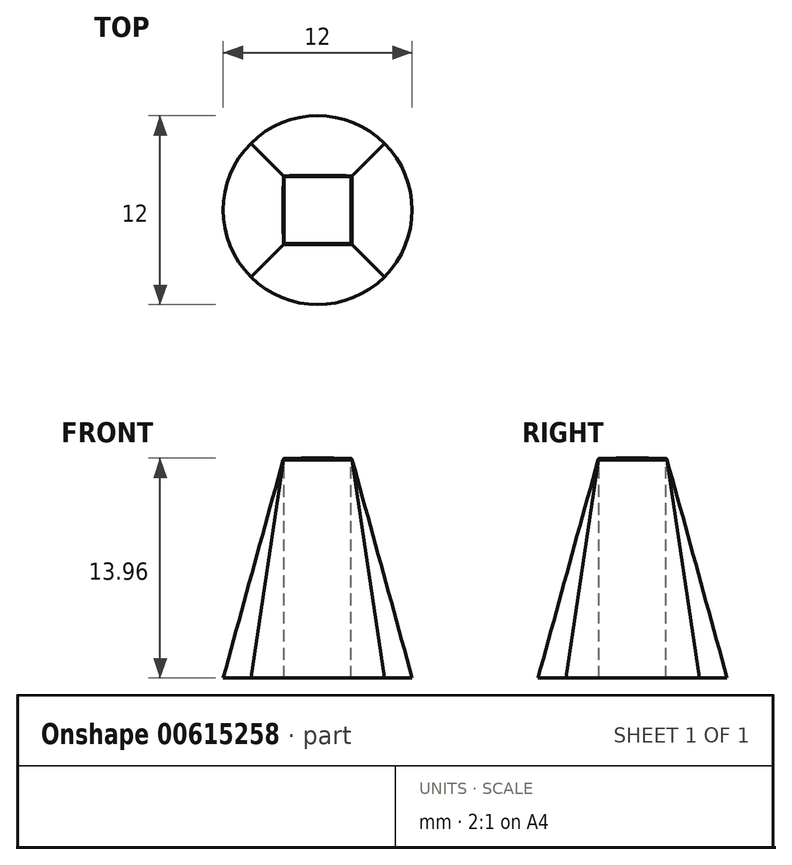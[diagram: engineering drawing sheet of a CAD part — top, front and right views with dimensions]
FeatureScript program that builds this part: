
annotation { "Feature Type Name" : "Feature", "Feature Type Description" : "" }
export const myFeature = defineFeature(function(context is Context, id is Id, definition is map)
    precondition{}
    {
        {
            var Q0;
            Q0=qCreatedBy(makeId("Top.planeOp"),FACE);
            var sketch = newSketch(context, id + "F0", { "sketchPlane" : qUnion([Q0])});
            skCircle(sketch, "E0", {"center": v(0, 0) * mm, "radius": 6 * mm});
            skSolve(sketch);
        }
        {
            var Q0;
            Q0=makeQuery(id+"F0.imprint","IMPRINT",FACE,{"disambiguationData":[TD([[makeQuery(id+"F0.imprint","IMPRINT",EDGE,{"derivedFrom":sQuery(id+"F0.wireOp",EDGE,"E0")}),1.0]])]});
            cPlane(context, id + "F1", {"entities" : qUnion([Q0]), "cplaneType" : CPlaneType.OFFSET, "offset" : 14 * mm, "width" : 150 * mm, "height" : 150 * mm});
        }
        {
            var Q0;
            Q0=qCreatedBy(id+"F1.planeOp",FACE);
            var sketch = newSketch(context, id + "F2", { "sketchPlane" : qUnion([Q0])});
            skLineSegment(sketch, "E1.bottom", {"start": v(2.15, -2.15) * mm, "end": v(-2.15, -2.15) * mm});
            skLineSegment(sketch, "E1.top", {"start": v(2.15, 2.15) * mm, "end": v(-2.15, 2.15) * mm});
            skLineSegment(sketch, "E1.left", {"start": v(2.15, -2.15) * mm, "end": v(2.15, 2.15) * mm});
            skLineSegment(sketch, "E1.right", {"start": v(-2.15, -2.15) * mm, "end": v(-2.15, 2.15) * mm});
            skPoint(sketch, "E1.middle", {"position": v(0, 0) * mm});
            skSolve(sketch);
        }
        {
            var Q0;
            Q0=makeQuery(id+"F0.imprint","IMPRINT",FACE,{"disambiguationData":[TD([[makeQuery(id+"F0.imprint","IMPRINT",EDGE,{"derivedFrom":sQuery(id+"F0.wireOp",EDGE,"E0")}),1.0]])]});
            var Q1;
            Q1=makeQuery(id+"F2.imprint","IMPRINT",FACE,{"disambiguationData":[TD([[makeQuery(id+"F2.imprint","IMPRINT",EDGE,{"derivedFrom":sQuery(id+"F2.wireOp",EDGE,"E1.bottom")}),-1.0]])]});
            loft(context, id + "F3", {"sheetProfilesArray" : [{ "sheetProfileEntities" : qUnion([Q0]) }, { "sheetProfileEntities" : qUnion([Q1]) }]});
        }
        {
            var Q0;
            Q0=makeQuery(id+"F3.opLoft","CAP_FACE",FACE,{"disambiguationData":[OSD([makeQuery(id+"F2.imprint","IMPRINT",FACE,{"disambiguationData":[TD([[makeQuery(id+"F2.imprint","IMPRINT",EDGE,{"derivedFrom":sQuery(id+"F2.wireOp",EDGE,"E1.bottom")}),-1.0]])]})])],"isStart":true});
            var sketch = newSketch(context, id + "F4", { "sketchPlane" : qUnion([Q0])});
            skLineSegment(sketch, "E2.bottom", {"start": v(2.13, -2.13) * mm, "end": v(-2.12, -2.13) * mm});
            skLineSegment(sketch, "E2.top", {"start": v(2.12, 2.13) * mm, "end": v(-2.13, 2.12) * mm});
            skLineSegment(sketch, "E2.left", {"start": v(2.13, -2.13) * mm, "end": v(2.12, 2.13) * mm});
            skLineSegment(sketch, "E2.right", {"start": v(-2.12, -2.13) * mm, "end": v(-2.13, 2.12) * mm});
            skPoint(sketch, "E2.middle", {"position": v(0, 0) * mm});
            skSolve(sketch);
        }
        {
            var Q0;
            Q0=makeQuery(id+"F4.imprint","IMPRINT",FACE,{"disambiguationData":[TD([[makeQuery(id+"F4.imprint","IMPRINT",EDGE,{"derivedFrom":sQuery(id+"F4.wireOp",EDGE,"E2.bottom")}),-1.0]])]});
            extrude(context, id + "F5", {"entities" : qUnion([Q0]), "operationType" : NewBodyOperationType.REMOVE, "oppositeDirection" : true, "depth" : 25 * mm, "offsetDistance" : 25 * mm});
        }
        {
            var Q0;
            Q0=makeQuery(id+"F3.opLoft","MID_CAP_EDGE",EDGE,{"disambiguationData":[OSD([sQuery(id+"F2.wireOp",EDGE,"E1.top"),sQuery(id+"F2.wireOp",EDGE,"E1.left"),sQuery(id+"F2.wireOp",EDGE,"E1.right")])],"capPos":1.0});
            var Q1;
            Q1=makeQuery(id+"F3.opLoft","MID_CAP_EDGE",EDGE,{"disambiguationData":[OSD([sQuery(id+"F2.wireOp",EDGE,"E1.bottom"),sQuery(id+"F2.wireOp",EDGE,"E1.top"),sQuery(id+"F2.wireOp",EDGE,"E1.right")])],"capPos":1.0});
            var Q2;
            Q2=makeQuery(id+"F3.opLoft","MID_CAP_EDGE",EDGE,{"disambiguationData":[OSD([sQuery(id+"F2.wireOp",EDGE,"E1.bottom"),sQuery(id+"F2.wireOp",EDGE,"E1.left"),sQuery(id+"F2.wireOp",EDGE,"E1.right")])],"capPos":1.0});
            var Q3;
            Q3=makeQuery(id+"F3.opLoft","MID_CAP_EDGE",EDGE,{"disambiguationData":[OSD([sQuery(id+"F2.wireOp",EDGE,"E1.bottom"),sQuery(id+"F2.wireOp",EDGE,"E1.top"),sQuery(id+"F2.wireOp",EDGE,"E1.left")])],"capPos":1.0});
            fillet(context, id + "F6", {"entities" : qUnion([Q0, Q1, Q2, Q3]), "radius" : .2 * mm, "tangentPropagation" : true, "allowEdgeOverflow" : false});
        }
    });
